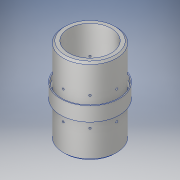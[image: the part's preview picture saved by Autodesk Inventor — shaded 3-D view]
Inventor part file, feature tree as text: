
AUTODESK INVENTOR PART (.ipt)
format: ipt  version: 2017 (Build 210142000, 142)  size: 225,792 bytes
history: native  units: in
note: dims shown in document units (in); Inventor stores cm internally (conversion verified against a paired STEP export)
features: sketch x6, extrude x5, plane x1, hole x1, pattern_circular x1, chamfer x1
ambient origin geometry x8: Origin, YZ Plane, XZ Plane, XY Plane, X Axis, Y Axis, Z Axis, Center Point
bodies: Solid1 (feature_tree)
feature tree (15):
  extrude  "Extrusion1"  Depth=4.0in
  extrude  "Extrusion2"  Depth=2.0in
  extrude  "Extrusion3"  Depth=5.0in TaperAngle=0.0deg
  plane  "Work Plane1"
  hole  "Hole1"  [1 undecoded]
  pattern_circular  "Circular Pattern1"  [2 undecoded]
  chamfer  "Chamfer1"  Distance=3.1496in Angle=360.0deg
  extrude  "Extrusion4"  Depth=0.25in TaperAngle=45.0deg
  extrude  "Extrusion5"  Depth=0.75in
  sketch  "Sketch1"  dims[d0=8.25in d1=4.0in]
  sketch  "Sketch2"  dims[d2=2.0in d3=0.0in d4=7.5in]
  sketch  "Sketch3"  dims[d5=6.0in d6=5.0in d7=0.0in]
  sketch  "Sketch4"  dims[d8=6.0in d9=7.5in]
  sketch  "Sketch5"  dims[d10=5.0in d11=0.0in]
  sketch  "Sketch6"  dims[d12=1.0in d13=1.0in d14=0.25in d15=0.75in d16=0.375in d17=0.25in d18=0.5635in d19=1.0in d20=0.8108in d21=3.1496in d22=360.0deg d24=0.25in d25=0.125in d26=45.0deg d27=8.0in d28=7.5in d29=0.75in d30=0.0in d31=8.0in d32=7.5in d33=0.75in d34=0.0in]
note: 3 required parameter values undecoded (feature->parameter linkage not recoverable at this tier; creation-order binding heuristic only, values carry confidence <= 0.55)
